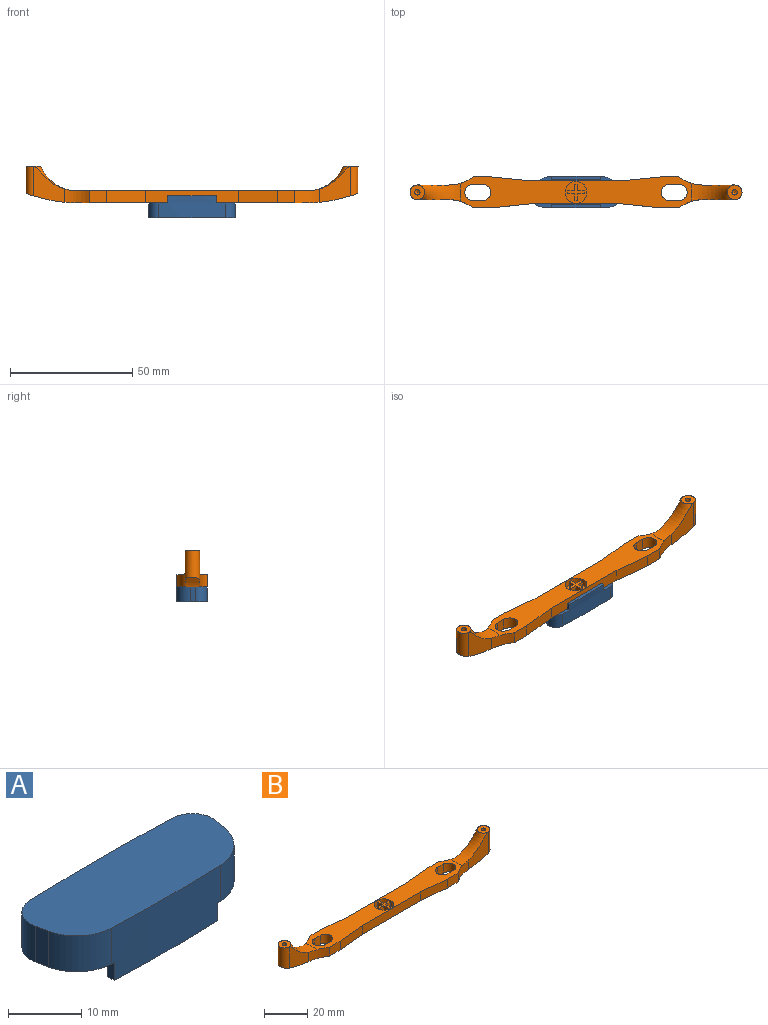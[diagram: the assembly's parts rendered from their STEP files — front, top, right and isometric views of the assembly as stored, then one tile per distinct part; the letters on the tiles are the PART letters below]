
ASSEMBLY  parts=2 mates=1
PART A: 18 faces, bbox 35.3x13x9 mm
  f0: plane 35.26x12.66mm, normal (0,0,-1), area 358.1mm2, adj f1,f2,f3,f4,f5,f6,f7,f8
  f1: plane 6x2.13mm, normal (0.98,-0.2,0), area 13mm2, adj f0,f2,f8,f9
  f2: cylinder r=4mm len=6mm, axis (0,0,-1), area 41.7mm2, adj f0,f1,f3,f9
  f3: cylinder r=342.5mm len=27.58mm, axis (0,0,-1), area 225.5mm2, adj f0,f2,f4,f9,f11,f12,f13
  f4: cylinder r=4mm len=6mm, axis (0,0,-1), area 41.7mm2, adj f0,f3,f5,f9
  f5: plane 6x2.13mm, normal (-0.98,-0.2,0), area 13mm2, adj f0,f4,f6,f9
  f6: cylinder r=7mm len=6.57mm, axis (0,0,-1), area 55.6mm2, adj f0,f5,f7,f9
  f7: cylinder r=256.25mm len=21.07mm, axis (0,0,-1), area 186.5mm2, adj f0,f6,f8,f9,f14,f16,f17
  f8: cylinder r=7mm len=6.57mm, axis (0,0,-1), area 55.6mm2, adj f0,f1,f7,f9
  f9: plane 35.26x13mm, normal (0,0,1), area 415.8mm2, adj f1,f2,f3,f4,f5,f6,f7,f8
  f10: plane 20x3mm, normal (0,-1,0), area 60mm2, adj f0,f11,f12,f13
  f11: plane 3x1.35mm, normal (-1,0,0), area 4.1mm2, adj f0,f3,f10,f13
  f12: plane 3x1.35mm, normal (1,0,0), area 4.1mm2, adj f0,f3,f10,f13
  f13: plane 20x1.5mm, normal (0,0,-1), area 29mm2, adj f3,f10,f11,f12
  f14: plane 3x1.31mm, normal (-1,0,0), area 3.9mm2, adj f0,f7,f15,f17
  f15: plane 20x3mm, normal (0,1,0), area 60mm2, adj f0,f14,f16,f17
  f16: plane 3x1.31mm, normal (1,0,0), area 3.9mm2, adj f0,f7,f15,f17
  f17: plane 20x1.5mm, normal (0,0,-1), area 28.7mm2, adj f7,f14,f15,f16
PART B: 55 faces, bbox 136x63.2x21 mm
  f0: plane 14.74x12.9mm, normal (0,1,0), area 107.7mm2, adj f1,f9,f33,f53
  f1: cylinder r=3mm len=12.06mm, axis (0,0,-1), area 107.4mm2, adj f0,f2,f30,f53
  f2: plane 14.74x12.9mm, normal (0,-1,0), area 107.7mm2, adj f1,f3,f33,f53
  f3: cylinder r=16.5mm len=10mm, axis (0,0,-1), area 54.6mm2, adj f2,f10,f17,f29,f33,f53
  f4: cylinder r=16.5mm len=10mm, axis (0,0,-1), area 54.6mm2, adj f5,f10,f21,f29,f32,f54
  f5: plane 14.74x12.9mm, normal (0,-1,0), area 107.7mm2, adj f4,f6,f32,f54
  f6: cylinder r=3mm len=12.06mm, axis (0,0,-1), area 107.4mm2, adj f5,f7,f31,f54
  f7: plane 14.74x12.9mm, normal (0,1,0), area 107.7mm2, adj f6,f8,f32,f54
  f8: cylinder r=16.5mm len=10mm, axis (0,0,-1), area 54.6mm2, adj f7,f10,f22,f29,f32,f54
  f9: cylinder r=16.5mm len=10mm, axis (0,0,-1), area 54.6mm2, adj f0,f10,f26,f29,f33,f53
  f10: plane 94.76x12.75mm, normal (0,0,-1), area 877.1mm2, adj f3,f4,f8,f9,f11,f12,f13,f14
  f11: plane 5x3.7mm, normal (0,1,0), area 18.5mm2, adj f10,f12,f28,f29
  f12: cylinder r=3.4mm len=6.8mm, axis (0,0,-1), area 53.4mm2, adj f10,f11,f13,f29
  f13: plane 5x3.7mm, normal (0,-1,0), area 18.5mm2, adj f10,f12,f28,f29
  f14: cylinder r=3.4mm len=6.8mm, axis (0,0,-1), area 53.4mm2, adj f10,f15,f27,f29
  f15: plane 5x3.7mm, normal (0,1,0), area 18.5mm2, adj f10,f14,f16,f29
  f16: cylinder r=3.4mm len=6.8mm, axis (0,0,-1), area 53.4mm2, adj f10,f15,f27,f29
  f17: plane 7.1x5mm, normal (0,-1,0), area 35.5mm2, adj f3,f10,f18,f29
  f18: plane 16x5mm, normal (0.1,-0.99,0), area 80.4mm2, adj f10,f17,f19,f29
  f19: plane 38x5mm, normal (0,-1,0), area 190mm2, adj f10,f18,f20,f29
  f20: plane 16x5mm, normal (-0.1,-0.99,0), area 80.4mm2, adj f10,f19,f21,f29
  f21: plane 7.1x5mm, normal (0,-1,0), area 35.5mm2, adj f4,f10,f20,f29
  f22: plane 7.1x5mm, normal (0,1,0), area 35.5mm2, adj f8,f10,f23,f29
  f23: plane 16x5mm, normal (-0.1,0.99,0), area 80.4mm2, adj f10,f22,f24,f29
  f24: plane 38x5mm, normal (0,1,0), area 190mm2, adj f10,f23,f25,f29
  f25: plane 16x5mm, normal (0.1,0.99,0), area 80.4mm2, adj f10,f24,f26,f29
  f26: plane 7.1x5mm, normal (0,1,0), area 35.5mm2, adj f9,f10,f25,f29
  f27: plane 5x3.7mm, normal (0,-1,0), area 18.5mm2, adj f10,f14,f16,f29
  f28: cylinder r=3.4mm len=6.8mm, axis (0,0,-1), area 53.4mm2, adj f10,f11,f13,f29
  f29: plane 95.09x12.75mm, normal (0,0,1), area 812.3mm2, adj f3,f4,f8,f9,f11,f12,f13,f14
  f30: plane 6x6mm, normal (0,0,1), area 24.5mm2, adj f1,f33,f37
  f31: plane 6x6mm, normal (0,0,1), area 24.5mm2, adj f6,f32,f35
  f32: torus R=17.83mm, axis (0,0,1), area 122mm2, adj f4,f5,f7,f8,f29,f31
  f33: torus R=17.83mm, axis (0,0,1), area 122mm2, adj f0,f2,f3,f9,f29,f30
  f34: cone r=0mm half-angle=59deg, axis (0,0,1), area 4.4mm2, adj f35
  f35: cylinder r=1.1mm len=10mm, axis (0,0,1), area 69.1mm2, adj f31,f34
  f36: cone r=0mm half-angle=59deg, axis (0,0,1), area 4.4mm2, adj f37
  f37: cylinder r=1.1mm len=10mm, axis (0,0,1), area 69.1mm2, adj f30,f36
  f38: plane 3x2.8mm, normal (0,1,0), area 8.4mm2, adj f39,f49,f51,f52
  f39: plane 3x2.8mm, normal (-1,0,0), area 8.4mm2, adj f38,f40,f51,f52
  f40: plane 3x1.2mm, normal (0,1,0), area 3.6mm2, adj f39,f41,f51,f52
  f41: plane 3x2.8mm, normal (1,0,0), area 8.4mm2, adj f40,f42,f51,f52
  f42: plane 3x2.8mm, normal (0,1,0), area 8.4mm2, adj f41,f43,f51,f52
  f43: plane 3x1.2mm, normal (1,0,0), area 3.6mm2, adj f42,f44,f51,f52
  f44: plane 3x2.8mm, normal (0,-1,0), area 8.4mm2, adj f43,f45,f51,f52
  f45: plane 3x2.8mm, normal (1,0,0), area 8.4mm2, adj f44,f46,f51,f52
  f46: plane 3x1.2mm, normal (0,-1,0), area 3.6mm2, adj f45,f47,f51,f52
  f47: plane 3x2.8mm, normal (-1,0,0), area 8.4mm2, adj f46,f48,f51,f52
  f48: plane 3x2.8mm, normal (0,-1,0), area 8.4mm2, adj f47,f49,f51,f52
  f49: plane 3x1.2mm, normal (-1,0,0), area 3.6mm2, adj f38,f48,f51,f52
  f50: cylinder r=4.5mm len=9mm, axis (0,0,1), area 84.8mm2, adj f29,f51
  f51: plane 9x9mm, normal (0,0,1), area 48.7mm2, adj f38,f39,f40,f41,f42,f43,f44,f45
  f52: plane 6.8x6.8mm, normal (0,0,1), area 14.9mm2, adj f38,f39,f40,f41,f42,f43,f44,f45
  f53: cylinder r=60mm len=20.62mm, axis (0,-1,0), area 125.8mm2, adj f0,f1,f2,f3,f9,f10
  f54: cylinder r=60mm len=20.62mm, axis (0,-1,0), area 125.8mm2, adj f4,f5,f6,f7,f8,f10
PLACE A rot(axis=(1,0,0),180deg) t=(-24.98,-10.51,12.96)mm
PLACE B t=(-24.98,-10.72,12.96)mm
MATE fastened A.f0 <-> B.f50  axis (0,0,1) through (-24.98,-10.72,12.96)mm
